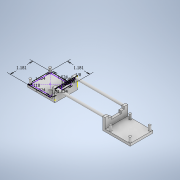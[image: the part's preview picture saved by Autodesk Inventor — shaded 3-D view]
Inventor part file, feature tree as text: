
AUTODESK INVENTOR PART (.ipt)
format: ipt  version: 2020 (Build 240168000, 168)  size: 195,584 bytes
history: native  units: in
note: dims shown in document units (in); Inventor stores cm internally (conversion verified against a paired STEP export)
features: extrude x6, sketch x4, mirror x1
ambient origin geometry x8: Origin, YZ Plane, XZ Plane, XY Plane, X Axis, Y Axis, Z Axis, Center Point
bodies: Solid1 (feature_tree)
feature tree (11):
  sketch  "Sketch1"  dims[d0=1.1811in d1=1.1811in]
  extrude  "Extrusion1"  Depth=1.1811in
  extrude  "Extrusion2"  Depth=1.0236in
  extrude  "Extrusion3"  Depth=0.7874in
  extrude  "Extrusion4"  Depth=0.25in TaperAngle=0.0deg
  sketch  "Sketch4"  dims[d13=0.125in d14=0.0in d15=0.25in d16=0.0in d17=0.25in d18=0.0in d19=0.125in d20=0.5187in d21=0.0in d22=0.0625in d23=0.5in d24=90.0deg d25=1.0in d26=0.125in d27=0.125in d28=1.25in d29=0.0in d30=0.125in d31=0.0in]
  extrude  "Extrusion5"  Depth=0.25in TaperAngle=0.0deg
  extrude  "Extrusion6"  Depth=0.125in
  mirror  "Mirror1"
  sketch  "Sketch2"  dims[d2=1.0236in d3=1.0236in]
  sketch  "Sketch3"  dims[d4=0.1181in d5=0.7874in d7=1.0236in d8=0.7874in d10=1.0236in]
